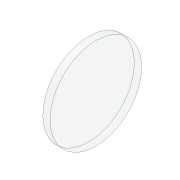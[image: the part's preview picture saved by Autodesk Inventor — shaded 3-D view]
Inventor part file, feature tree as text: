
AUTODESK INVENTOR PART (.ipt)
format: ipt  version: 2020.3 (Build 243373000, 373)  size: 82,944 bytes
history: native  units: mm
features: revolve x1, sketch x1
ambient origin geometry x8: Origin, YZ Plane, XZ Plane, XY Plane, X Axis, Y Axis, Z Axis, Center Point
bodies: Solid1 (feature_tree)
feature tree (2):
  revolve  "Revolution1"  [1 undecoded]
  sketch  "Sketch1"  dims[d0=25.0mm d1=4.0mm d2=50.0mm d3=130.0mm d4=90.0deg]
note: 1 required parameter value undecoded (feature->parameter linkage not recoverable at this tier; creation-order binding heuristic only, values carry confidence <= 0.55)
